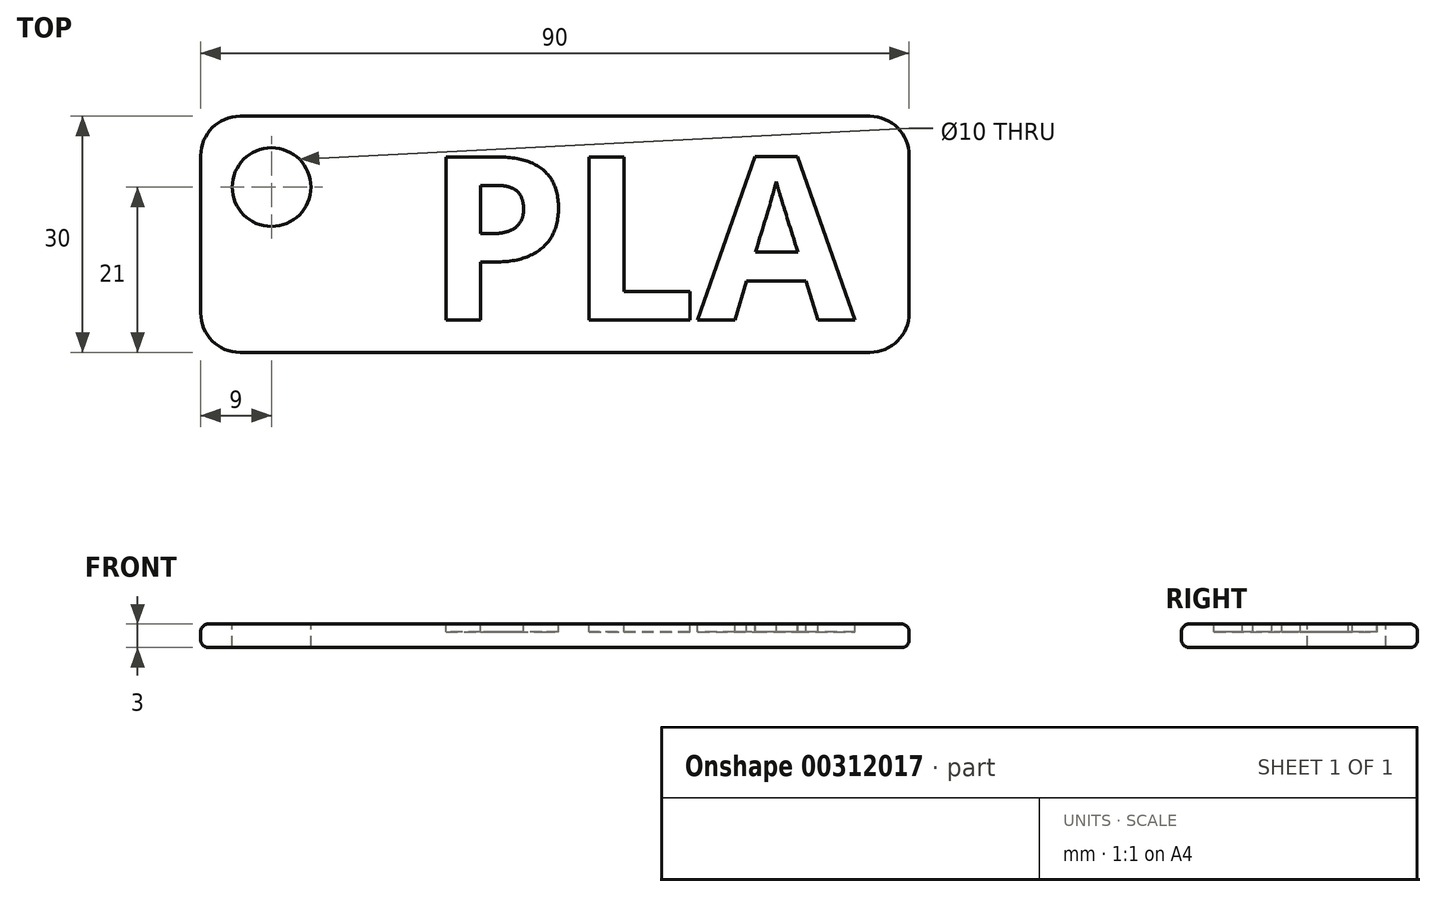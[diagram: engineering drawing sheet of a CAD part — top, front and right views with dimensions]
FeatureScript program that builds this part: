
annotation { "Feature Type Name" : "Feature", "Feature Type Description" : "" }
export const myFeature = defineFeature(function(context is Context, id is Id, definition is map)
    precondition{}
    {
        {
            var Q0;
            Q0=qCreatedBy(makeId("Top.planeOp"),FACE);
            var sketch = newSketch(context, id + "F0", { "sketchPlane" : qUnion([Q0])});
            skLineSegment(sketch, "E0.bottom", {"start": v(-45, 15) * mm, "end": v(45, 15) * mm});
            skLineSegment(sketch, "E0.top", {"start": v(-45, -15) * mm, "end": v(45, -15) * mm});
            skLineSegment(sketch, "E0.left", {"start": v(-45, 15) * mm, "end": v(-45, -15) * mm});
            skLineSegment(sketch, "E0.right", {"start": v(45, 15) * mm, "end": v(45, -15) * mm});
            skLineSegment(sketch, "E1", {"start": v(-45, 15) * mm, "end": v(45, -15) * mm, "construction": true});
            skSolve(sketch);
        }
        {
            var Q0;
            Q0=makeQuery(id+"F0.imprint","IMPRINT",FACE,{"disambiguationData":[TD([[makeQuery(id+"F0.imprint","IMPRINT",EDGE,{"derivedFrom":sQuery(id+"F0.wireOp",EDGE,"E0.bottom")}),-1.0]])]});
            extrude(context, id + "F1", {"entities" : qUnion([Q0]), "depth" : 3 * mm});
        }
        {
            var Q0;
            Q0=makeQuery(id+"F1.opExtrude","CAP_FACE",FACE,{"disambiguationData":[OSD([sQuery(id+"F0.wireOp",EDGE,"E0.bottom"),sQuery(id+"F0.wireOp",EDGE,"E0.top"),sQuery(id+"F0.wireOp",EDGE,"E0.left"),sQuery(id+"F0.wireOp",EDGE,"E0.right")])],"isStart":false});
            var Q1;
            Q1=makeQuery(id+"F1.opExtrude","CAP_FACE",FACE,{"disambiguationData":[OSD([sQuery(id+"F0.wireOp",EDGE,"E0.bottom"),sQuery(id+"F0.wireOp",EDGE,"E0.top"),sQuery(id+"F0.wireOp",EDGE,"E0.left"),sQuery(id+"F0.wireOp",EDGE,"E0.right")])],"isStart":true});
            fillet(context, id + "F2", {"entities" : qUnion([Q0, Q1]), "radius" : 1 * mm, "tangentPropagation" : true, "allowEdgeOverflow" : false});
        }
        {
            var Q0;
            Q0=makeQuery(id+"F1.opExtrude","SWEPT_EDGE",EDGE,{"disambiguationData":[OSD([sQuery(id+"F0.wireOp",EDGE,"E0.top"),sQuery(id+"F0.wireOp",EDGE,"E0.right")])]});
            var Q1;
            Q1=makeQuery(id+"F1.opExtrude","SWEPT_EDGE",EDGE,{"disambiguationData":[OSD([sQuery(id+"F0.wireOp",EDGE,"E0.bottom"),sQuery(id+"F0.wireOp",EDGE,"E0.right")])]});
            var Q2;
            Q2=makeQuery(id+"F1.opExtrude","SWEPT_EDGE",EDGE,{"disambiguationData":[OSD([sQuery(id+"F0.wireOp",EDGE,"E0.bottom"),sQuery(id+"F0.wireOp",EDGE,"E0.left")])]});
            var Q3;
            Q3=makeQuery(id+"F1.opExtrude","SWEPT_EDGE",EDGE,{"disambiguationData":[OSD([sQuery(id+"F0.wireOp",EDGE,"E0.top"),sQuery(id+"F0.wireOp",EDGE,"E0.left")])]});
            fillet(context, id + "F3", {"entities" : qUnion([Q0, Q1, Q2, Q3]), "radius" : 5 * mm, "tangentPropagation" : true, "allowEdgeOverflow" : false});
        }
        {
            var Q0;
            {var subQ0=sQuery(id+"F0.wireOp",EDGE,"E0.left");var subQ2=sQuery(id+"F0.wireOp",EDGE,"E0.bottom");var subQ4=sQuery(id+"F0.wireOp",EDGE,"E0.right");var subQ6=sQuery(id+"F0.wireOp",EDGE,"E0.top");Q0=makeQuery(id+"FmQCBBX3Ub0qneL_1.boolean.opBoolean","SPLIT",FACE,{"disambiguationData":[TD([makeQuery(id+"FmQCBBX3Ub0qneL_1.opExtrude","SWEPT_FACE",FACE,{"disambiguationData":[OSD([sQuery(id+"FOCoeRmDbjhRCuz_1.wireOp",EDGE,"4a1fb44a-e7be-4e23-9449-000d953c446c.sketch_text.stroke-0")])]})])],"derivedFrom":makeQuery(id+"F1.opExtrude","CAP_FACE",FACE,{"disambiguationData":[OSD([subQ2,subQ6,subQ0,subQ4])],"isStart":false})});}
            var sketch = newSketch(context, id + "F4", { "sketchPlane" : qUnion([Q0])});
            skCircle(sketch, "E2", {"center": v(-36, 6) * mm, "radius": 5 * mm});
            skSolve(sketch);
        }
        {
            var Q0;
            Q0 = qSketchRegion(id + "F4", true);
            extrude(context, id + "F5", {"entities" : qUnion([Q0]), "operationType" : NewBodyOperationType.REMOVE, "oppositeDirection" : true, "depth" : 3 * mm});
        }
        {
            var Q0;
            Q0=makeQuery(id+"F1.opExtrude","CAP_FACE",FACE,{"disambiguationData":[OSD([sQuery(id+"F0.wireOp",EDGE,"E0.bottom"),sQuery(id+"F0.wireOp",EDGE,"E0.top"),sQuery(id+"F0.wireOp",EDGE,"E0.left"),sQuery(id+"F0.wireOp",EDGE,"E0.right")])],"isStart":false});
            var sketch = newSketch(context, id + "F6", { "sketchPlane" : qUnion([Q0])});
            skText(sketch, "E3", { "text": "PLA", "fontName": "OpenSans-Bold.ttf"});
            const initialGuessF6  = {"E3": [-0.01645, -0.01087, 1, 0, 0.02087]};
            skSetInitialGuess(sketch, initialGuessF6);
            skSolve(sketch);
        }
        {
            var Q0;
            Q0 = qSketchRegion(id + "F6", true);
            extrude(context, id + "F7", {"entities" : qUnion([Q0]), "operationType" : NewBodyOperationType.REMOVE, "oppositeDirection" : true, "depth" : 1 * mm});
        }
    });
